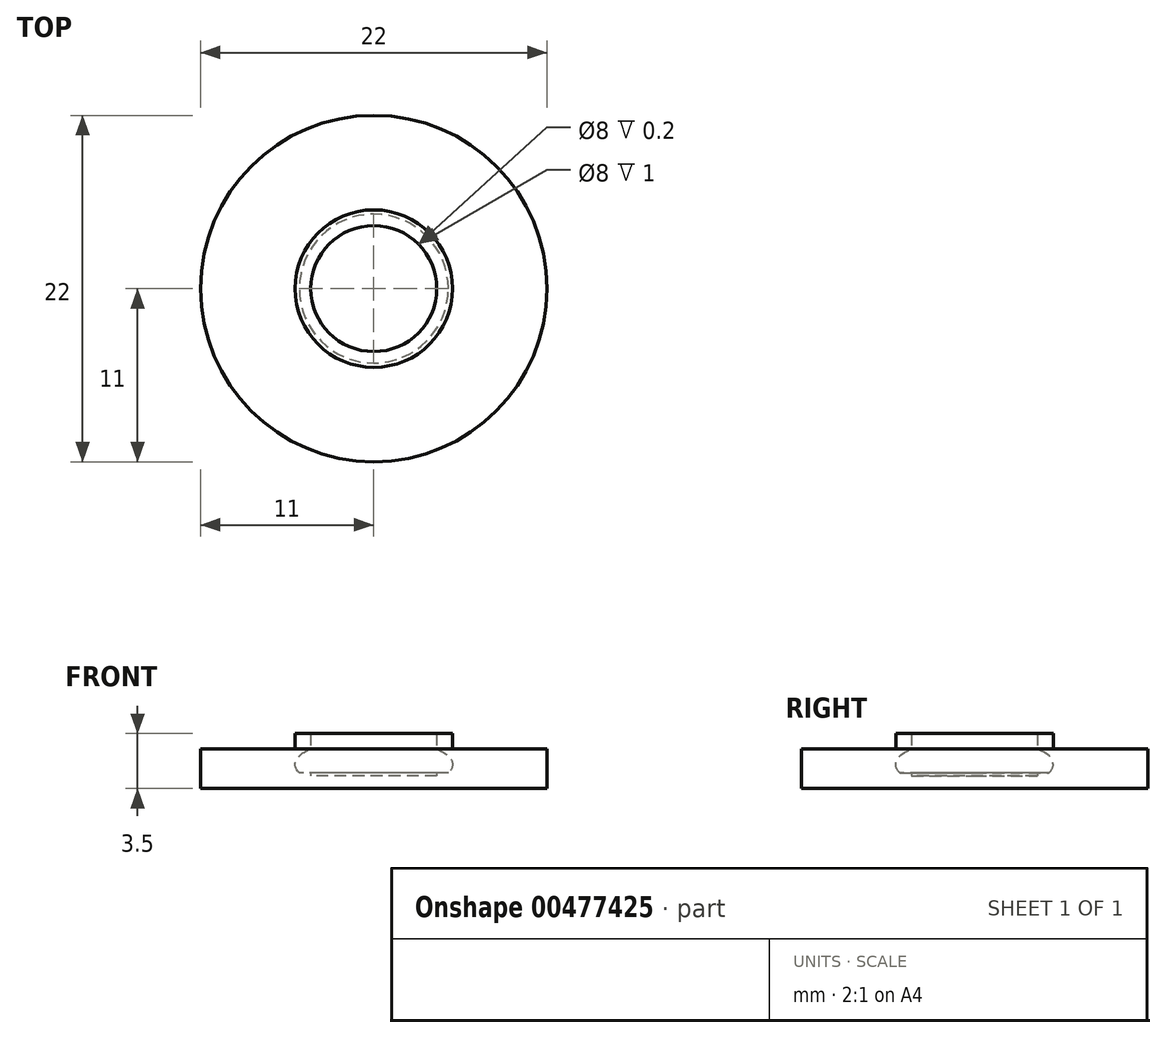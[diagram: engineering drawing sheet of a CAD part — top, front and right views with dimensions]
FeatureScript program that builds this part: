
annotation { "Feature Type Name" : "Feature", "Feature Type Description" : "" }
export const myFeature = defineFeature(function(context is Context, id is Id, definition is map)
    precondition{}
    {
        {
            var Q0;
            Q0=qCreatedBy(makeId("Top.planeOp"),FACE);
            var sketch = newSketch(context, id + "F0", { "sketchPlane" : qUnion([Q0])});
            skCircle(sketch, "E0", {"center": v(0, 0) * mm, "radius": 11 * mm});
            skCircle(sketch, "E1", {"center": v(0, 0) * mm, "radius": 4 * mm});
            skCircle(sketch, "E2.0", {"center": v(0, 0) * mm, "radius": 3.9 * mm});
            skSolve(sketch);
        }
        {
            var Q0;
            Q0=makeQuery(id+"F0.imprint","IMPRINT",FACE,{"disambiguationData":[TD([[makeQuery(id+"F0.imprint","IMPRINT",EDGE,{"derivedFrom":sQuery(id+"F0.wireOp",EDGE,"E0")}),1.0]])]});
            var Q1;
            Q1=sQuery(id+"F0.wireOp",EDGE,"E0");
            var Q2;
            Q2=sQuery(id+"F0.wireOp",EDGE,"E1");
            var Q3;
            Q3=sQuery(id+"F0.wireOp",EDGE,"E2.0");
            extrude(context, id + "F1", {"entities" : qUnion([Q0]), "surfaceEntities" : qUnion([Q1, Q2, Q3]), "depth" : 2.5 * mm});
        }
        {
            var Q0;
            Q0=makeQuery(id+"F0.imprint","IMPRINT",FACE,{"disambiguationData":[TD([[makeQuery(id+"F0.imprint","IMPRINT",EDGE,{"derivedFrom":sQuery(id+"F0.wireOp",EDGE,"E1")}),1.0]])]});
            var Q1;
            Q1=makeQuery(id+"F0.imprint","IMPRINT",FACE,{"disambiguationData":[TD([[makeQuery(id+"F0.imprint","IMPRINT",EDGE,{"derivedFrom":sQuery(id+"F0.wireOp",EDGE,"E2.0")}),1.0]])]});
            extrude(context, id + "F2", {"entities" : qUnion([Q0, Q1]), "operationType" : NewBodyOperationType.ADD, "depth" : 0.8 * mm});
        }
        {
            var Q0;
            Q0=qCreatedBy(makeId("Front.planeOp"),FACE);
            var sketch = newSketch(context, id + "F3", { "sketchPlane" : qUnion([Q0])});
            skFitSpline(sketch, "E3", {"points": [v(4, 2.5) * mm, v(5, 1.5) * mm, v(4, 0.5) * mm], "startDerivative": vector(4.82, -1.91) * mm, "endDerivative": vector(-4.73, -2.8) * mm});
            skLineSegment(sketch, "E4", {"start": v(0, 0) * mm, "end": v(0, 3.28) * mm});
            skLineSegment(sketch, "E5", {"start": v(4, 2.5) * mm, "end": v(4, 0.5) * mm});
            skSolve(sketch);
        }
        {
            var Q0;
            Q0 = qSketchRegion(id + "F3", true);
            var Q1;
            Q1=sQuery(id+"F3.wireOp",EDGE,"E4");
            revolve(context, id + "F4", {"operationType" : NewBodyOperationType.REMOVE, "entities" : qUnion([Q0]), "axis" : qUnion([Q1]), "revolveType" : RevolveType.FULL, "oppositeDirection" : true});
        }
        {
            var Q0;
            Q0=makeQuery(id+"F1.opExtrude","CAP_FACE",FACE,{"disambiguationData":[OSD([sQuery(id+"F0.wireOp",EDGE,"E0"),sQuery(id+"F0.wireOp",EDGE,"E1")])],"isStart":false});
            var sketch = newSketch(context, id + "F5", { "sketchPlane" : qUnion([Q0])});
            skCircle(sketch, "E6", {"center": v(0, 0) * mm, "radius": 4 * mm});
            skCircle(sketch, "E7.0", {"center": v(0, 0) * mm, "radius": 5 * mm});
            skSolve(sketch);
        }
        {
            var Q0;
            Q0 = qSketchRegion(id + "F5", true);
            var Q1;
            Q1 = qSketchRegion(id + "F0", true);
            extrude(context, id + "F6", {"entities" : qUnion([Q0, Q1]), "operationType" : NewBodyOperationType.ADD, "depth" : 1 * mm});
        }
    });
